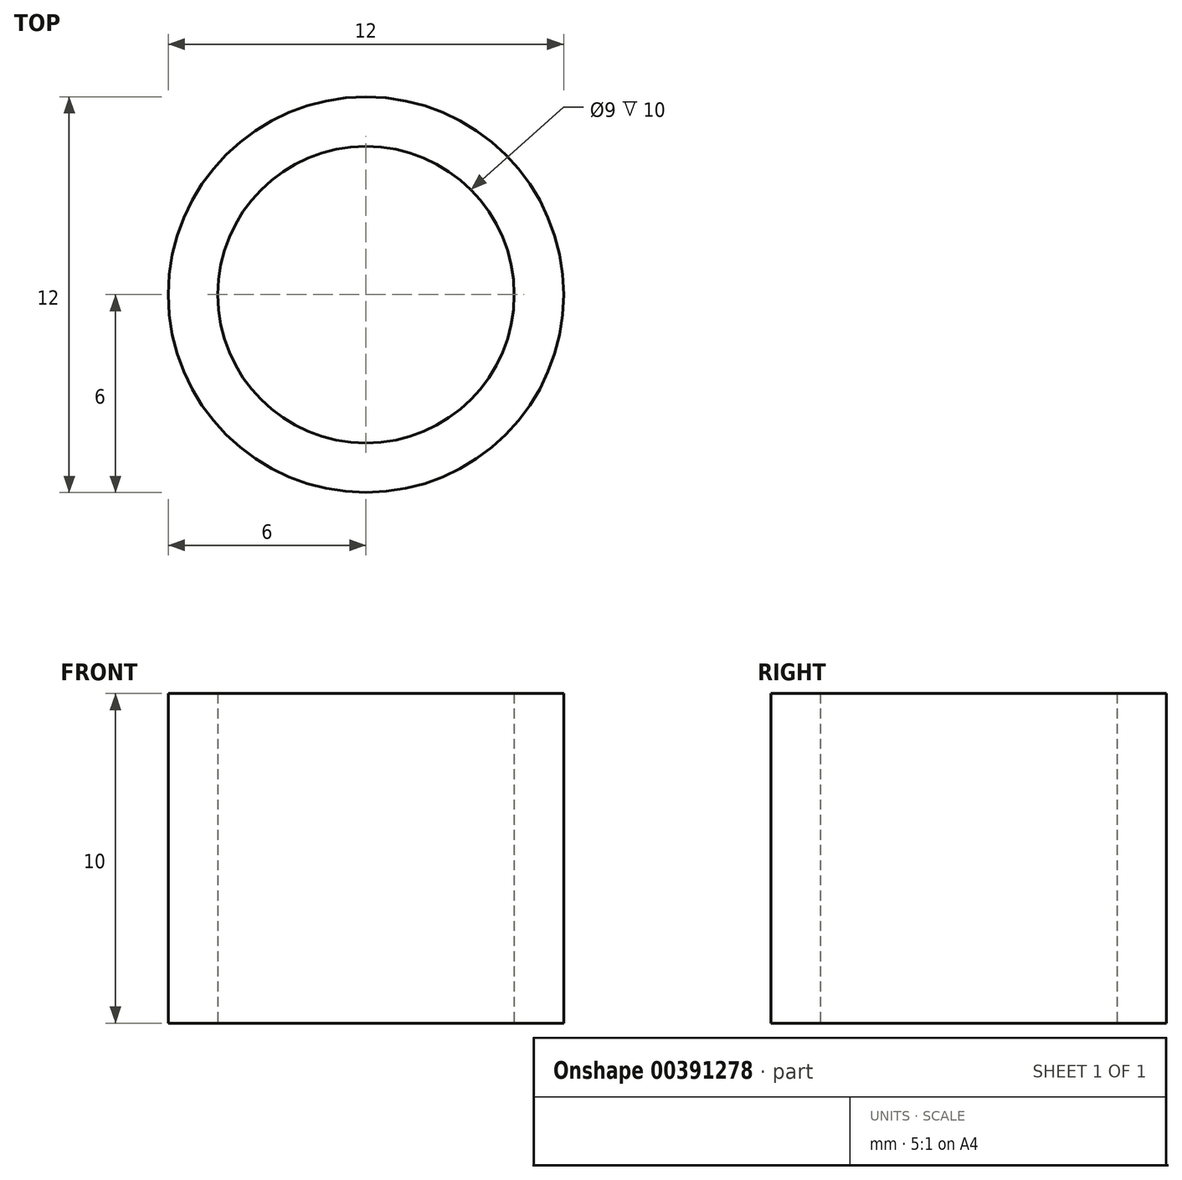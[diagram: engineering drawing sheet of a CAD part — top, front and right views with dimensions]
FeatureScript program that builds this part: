
annotation { "Feature Type Name" : "Feature", "Feature Type Description" : "" }
export const myFeature = defineFeature(function(context is Context, id is Id, definition is map)
    precondition{}
    {
        {
            var Q0;
            Q0=qCreatedBy(makeId("Top.planeOp"),FACE);
            var sketch = newSketch(context, id + "F0", { "sketchPlane" : qUnion([Q0])});
            skCircle(sketch, "E0", {"center": v(0, 0) * mm, "radius": 4.5 * mm});
            skCircle(sketch, "E1", {"center": v(0, 0) * mm, "radius": 6 * mm});
            skSolve(sketch);
        }
        {
            var Q0;
            Q0=makeQuery(id+"F0.imprint","IMPRINT",FACE,{"disambiguationData":[TD([[makeQuery(id+"F0.imprint","IMPRINT",EDGE,{"derivedFrom":sQuery(id+"F0.wireOp",EDGE,"E0")}),-1.0]])]});
            extrude(context, id + "F1", {"entities" : qUnion([Q0]), "depth" : 10 * mm});
        }
    });
